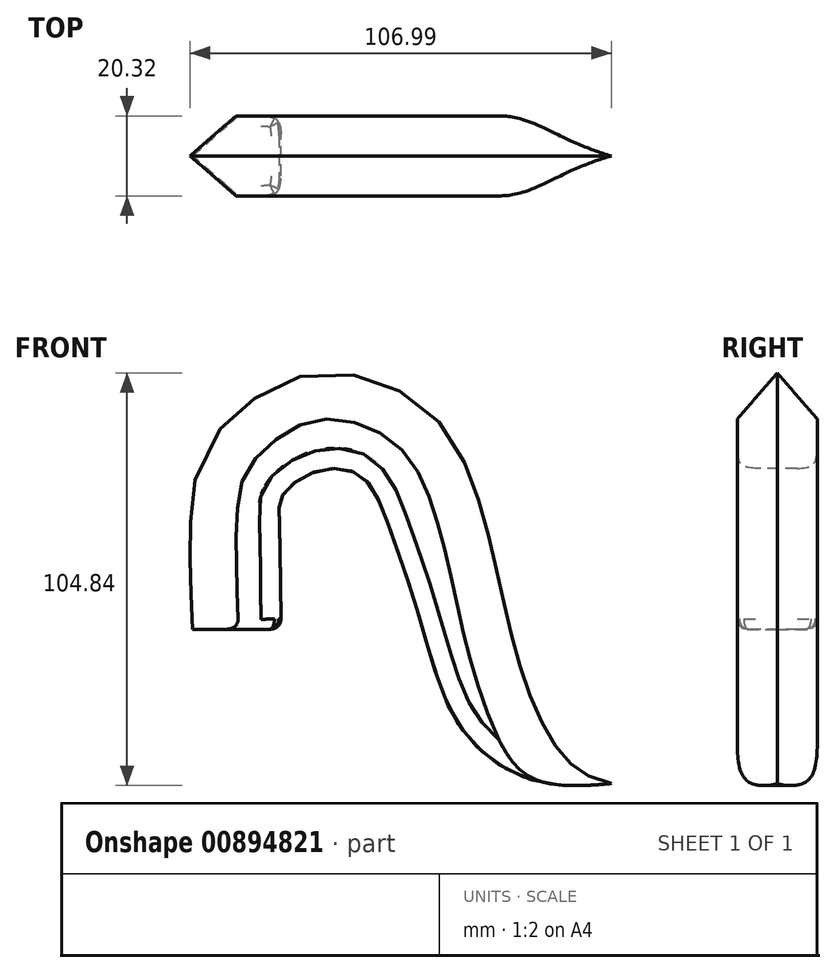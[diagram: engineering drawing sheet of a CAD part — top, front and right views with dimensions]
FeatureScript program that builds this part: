
annotation { "Feature Type Name" : "Feature", "Feature Type Description" : "" }
export const myFeature = defineFeature(function(context is Context, id is Id, definition is map)
    precondition{}
    {
        {
            var Q0;
            Q0=qCreatedBy(makeId("Front.planeOp"),FACE);
            var sketch = newSketch(context, id + "F0", { "sketchPlane" : qUnion([Q0])});
            skFitSpline(sketch, "E0", {"points": [v(97.64, 312.3) * mm, v(85.09, 317.57) * mm, v(70.5, 348.35) * mm, v(54.7, 400.2) * mm, v(30.81, 416.4) * mm, v(10.56, 414.77) * mm, v(-6.05, 402.22) * mm, v(-12.53, 387.64) * mm, v(-12.93, 351.18) * mm], "startDerivative": vector(-146.39, 31.52) * mm, "endDerivative": vector(11.6, -279.65) * mm});
            skFitSpline(sketch, "E1", {"points": [v(10.56, 351.18) * mm, v(10.15, 379.13) * mm, v(10.96, 385.2) * mm, v(19.47, 391.28) * mm, v(30.4, 390.47) * mm, v(37.3, 379.13) * mm, v(46.6, 351.18) * mm, v(56.33, 326.07) * mm, v(74.96, 312.7) * mm, v(97.64, 312.3) * mm], "startDerivative": vector(-1.94, 239.14) * mm, "endDerivative": vector(185.15, 19.41) * mm});
            skLineSegment(sketch, "E2", {"start": v(10.56, 351.18) * mm, "end": v(10.47, 10.97) * mm});
            skLineSegment(sketch, "E3", {"start": v(10.47, 10.97) * mm, "end": v(10.56, 351.18) * mm});
            skLineSegment(sketch, "E4", {"start": v(-12.93, 351.18) * mm, "end": v(-12.93, 10.97) * mm});
            skLineSegment(sketch, "E5", {"start": v(-12.93, 10.97) * mm, "end": v(10.47, 10.97) * mm});
            skLineSegment(sketch, "E6", {"start": v(10.56, 351.18) * mm, "end": v(-12.93, 351.18) * mm});
            skSolve(sketch);
        }
        {
            var Q0;
            Q0=makeQuery(id+"F0.imprint","IMPRINT",FACE,{"disambiguationData":[TD([[makeQuery(id+"F0.imprint","IMPRINT",EDGE,{"derivedFrom":sQuery(id+"F0.wireOp",EDGE,"E0")}),1.0]])]});
            extrude(context, id + "F1", {"entities" : qUnion([Q0]), "depth" : 10.16 * mm, "offsetDistance" : 25.4 * mm});
        }
        {
            var Q0;
            Q0=makeQuery(id+"F1.opExtrude","CAP_FACE",FACE,{"disambiguationData":[OSD([sQuery(id+"F0.wireOp",EDGE,"E0"),sQuery(id+"F0.wireOp",EDGE,"E1"),sQuery(id+"F0.wireOp",EDGE,"E3"),sQuery(id+"F0.wireOp",EDGE,"E4"),sQuery(id+"F0.wireOp",EDGE,"E5")])],"isStart":true});
            extrude(context, id + "F2", {"entities" : qUnion([Q0]), "operationType" : NewBodyOperationType.ADD, "depth" : 10.16 * mm, "offsetDistance" : 25.4 * mm});
        }
        {
            var Q0;
            Q0=makeQuery(id+"F1.opExtrude","CAP_EDGE",EDGE,{"disambiguationData":[OSD([sQuery(id+"F0.wireOp",EDGE,"E0")])],"isStart":false});
            var Q1;
            Q1=makeQuery(id+"F2.opExtrude","CAP_EDGE",EDGE,{"disambiguationData":[OSD([sQuery(id+"F0.wireOp",EDGE,"E0")])],"isStart":false});
            chamfer(context, id + "F3", {"entities" : qUnion([Q0, Q1]), "chamferType" : ChamferType.OFFSET_ANGLE, "width" : 12.7 * mm, "oppositeDirection" : false, "angle" : 41 * degree, "tangentPropagation" : true});
        }
        {
            var Q0;
            Q0=makeQuery(id+"F2.opExtrude","CAP_EDGE",EDGE,{"disambiguationData":[OSD([sQuery(id+"F0.wireOp",EDGE,"E1")])],"isStart":false});
            var Q1;
            Q1=makeQuery(id+"F1.opExtrude","CAP_EDGE",EDGE,{"disambiguationData":[OSD([sQuery(id+"F0.wireOp",EDGE,"E1")])],"isStart":false});
            fillet(context, id + "F4", {"entities" : qUnion([Q0, Q1]), "radius" : 5.08 * mm, "rho" : 0.6, "crossSection" : FilletCrossSection.CONIC, "allowEdgeOverflow" : false});
        }
        {
            var Q0;
            {var subQ0=sQuery(id+"F0.wireOp",EDGE,"E6");Q0=makeQuery(id+"F4.opFillet","BLEND_EDGE",EDGE,{"blendedFrom":[makeQuery(id+"F1.opExtrude","CAP_EDGE",EDGE,{"disambiguationData":[OSD([sQuery(id+"F0.wireOp",EDGE,"E1")])],"isStart":false}),makeQuery(id+"F2.boolean.opBoolean","MERGE",FACE,{"derivedFrom":[makeQuery(id+"F1.opExtrude","SWEPT_FACE",FACE,{"disambiguationData":[OSD([subQ0])]}),makeQuery(id+"F2.opExtrude","SWEPT_FACE",FACE,{"disambiguationData":[OSD([subQ0])]})]})],"blendedInto":[makeQuery(id+"F2.boolean.opBoolean","MERGE",FACE,{"derivedFrom":[makeQuery(id+"F1.opExtrude","SWEPT_FACE",FACE,{"disambiguationData":[OSD([subQ0])]}),makeQuery(id+"F2.opExtrude","SWEPT_FACE",FACE,{"disambiguationData":[OSD([subQ0])]})]})]});}
            var Q1;
            {var subQ0=sQuery(id+"F0.wireOp",EDGE,"E6");var subQ1=sQuery(id+"F0.wireOp",EDGE,"E3");var subQ2=sQuery(id+"F0.wireOp",EDGE,"E1");Q1=makeQuery(id+"F2.boolean.opBoolean","MERGE",EDGE,{"derivedFrom":[makeQuery(id+"F1.opExtrude","SWEPT_EDGE",EDGE,{"disambiguationData":[OSD([subQ2,subQ1,subQ0])]}),makeQuery(id+"F2.opExtrude","SWEPT_EDGE",EDGE,{"disambiguationData":[OSD([subQ2,subQ1,subQ0])]})]});}
            var Q2;
            {var subQ0=sQuery(id+"F0.wireOp",EDGE,"E6");Q2=makeQuery(id+"F4.opFillet","BLEND_EDGE",EDGE,{"blendedFrom":[makeQuery(id+"F2.opExtrude","CAP_EDGE",EDGE,{"disambiguationData":[OSD([sQuery(id+"F0.wireOp",EDGE,"E1")])],"isStart":false}),makeQuery(id+"F2.boolean.opBoolean","MERGE",FACE,{"derivedFrom":[makeQuery(id+"F1.opExtrude","SWEPT_FACE",FACE,{"disambiguationData":[OSD([subQ0])]}),makeQuery(id+"F2.opExtrude","SWEPT_FACE",FACE,{"disambiguationData":[OSD([subQ0])]})]})],"blendedInto":[makeQuery(id+"F2.boolean.opBoolean","MERGE",FACE,{"derivedFrom":[makeQuery(id+"F1.opExtrude","SWEPT_FACE",FACE,{"disambiguationData":[OSD([subQ0])]}),makeQuery(id+"F2.opExtrude","SWEPT_FACE",FACE,{"disambiguationData":[OSD([subQ0])]})]})]});}
            fillet(context, id + "F5", {"entities" : qUnion([Q0, Q1, Q2]), "radius" : 2.54 * mm, "tangentPropagation" : true, "allowEdgeOverflow" : false});
        }
    });
